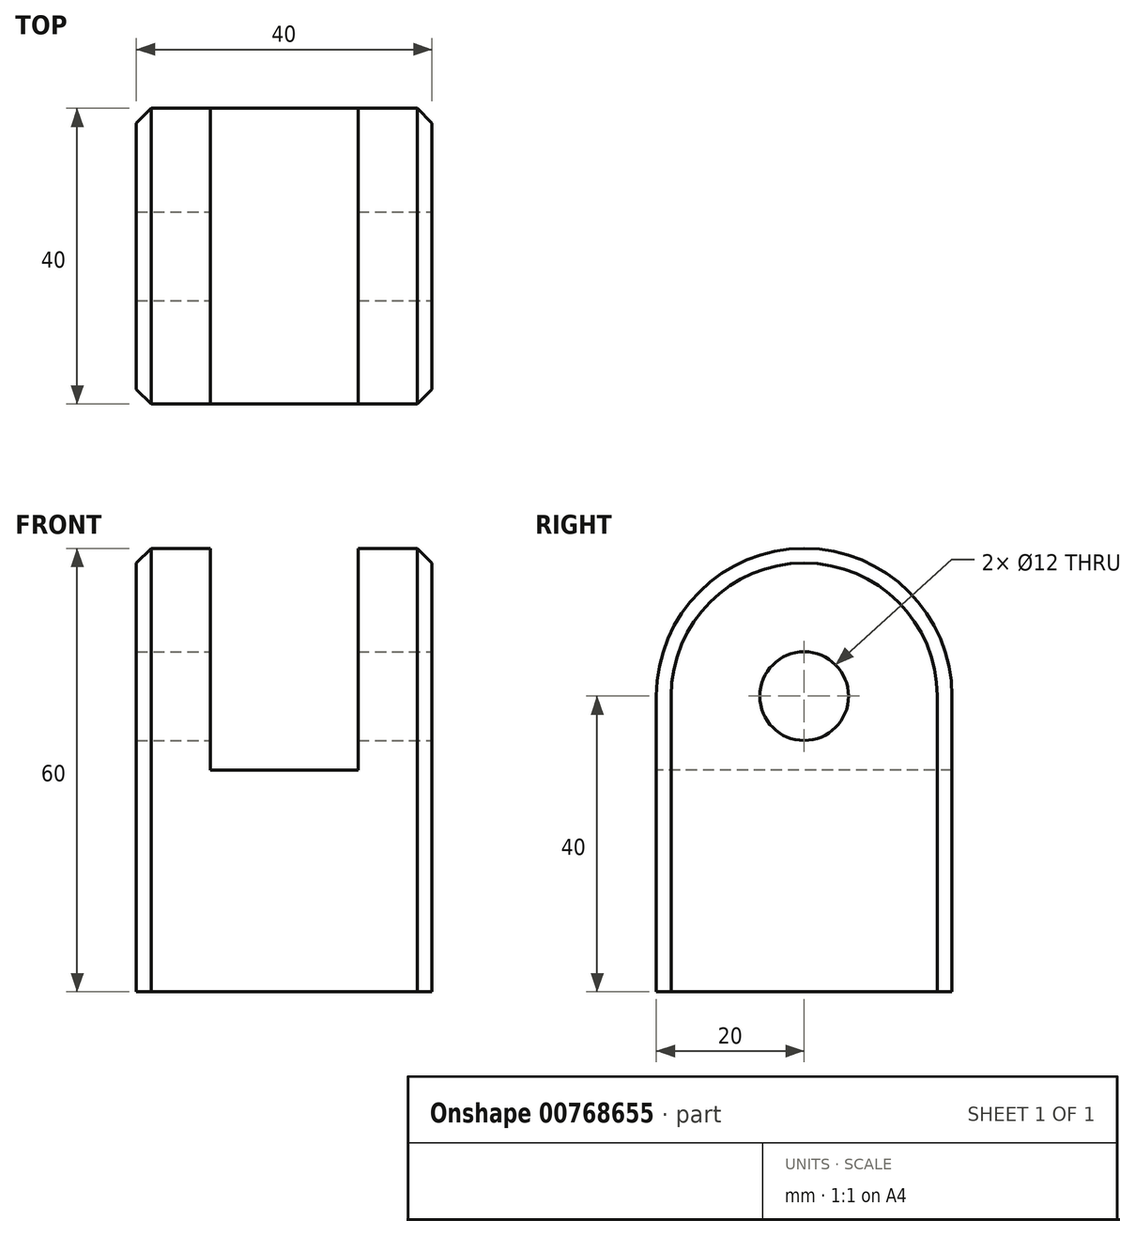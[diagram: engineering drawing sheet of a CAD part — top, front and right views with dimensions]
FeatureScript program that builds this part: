
annotation { "Feature Type Name" : "Feature", "Feature Type Description" : "" }
export const myFeature = defineFeature(function(context is Context, id is Id, definition is map)
    precondition{}
    {
        {
            var Q0;
            Q0=qCreatedBy(makeId("Top.planeOp"),FACE);
            var sketch = newSketch(context, id + "F0", { "sketchPlane" : qUnion([Q0])});
            skLineSegment(sketch, "E0.bottom", {"start": v(20, -20) * mm, "end": v(-20, -20) * mm});
            skLineSegment(sketch, "E0.top", {"start": v(20, 20) * mm, "end": v(-20, 20) * mm});
            skLineSegment(sketch, "E0.left", {"start": v(20, -20) * mm, "end": v(20, 20) * mm});
            skLineSegment(sketch, "E0.right", {"start": v(-20, -20) * mm, "end": v(-20, 20) * mm});
            skPoint(sketch, "E0.middle", {"position": v(0, 0) * mm});
            skSolve(sketch);
        }
        {
            var Q0;
            Q0 = qSketchRegion(id + "F0", true);
            extrude(context, id + "F1", {"entities" : qUnion([Q0]), "depth" : 60 * mm, "offsetDistance" : 25 * mm});
        }
        {
            var Q0;
            Q0=makeQuery(id+"F1.opExtrude","CAP_FACE",FACE,{"disambiguationData":[OSD([sQuery(id+"F0.wireOp",EDGE,"E0.bottom"),sQuery(id+"F0.wireOp",EDGE,"E0.top"),sQuery(id+"F0.wireOp",EDGE,"E0.left"),sQuery(id+"F0.wireOp",EDGE,"E0.right")])],"isStart":false});
            var sketch = newSketch(context, id + "F2", { "sketchPlane" : qUnion([Q0])});
            skLineSegment(sketch, "E1.bottom", {"start": v(-10, 20) * mm, "end": v(10, 20) * mm});
            skLineSegment(sketch, "E1.top", {"start": v(-10, -20) * mm, "end": v(10, -20) * mm});
            skLineSegment(sketch, "E1.left", {"start": v(-10, 20) * mm, "end": v(-10, -20) * mm});
            skLineSegment(sketch, "E1.right", {"start": v(10, 20) * mm, "end": v(10, -20) * mm});
            skLineSegment(sketch, "E2", {"start": v(-20, 0) * mm, "end": v(-10, 0) * mm, "construction": true});
            skLineSegment(sketch, "E3", {"start": v(-10, 0) * mm, "end": v(10, 0) * mm, "construction": true});
            skLineSegment(sketch, "E4", {"start": v(10, 0) * mm, "end": v(20, 0) * mm, "construction": true});
            skSolve(sketch);
        }
        {
            var Q0;
            Q0=makeQuery(id+"F2.imprint","IMPRINT",FACE,{"disambiguationData":[TD([[makeQuery(id+"F2.imprint","IMPRINT",EDGE,{"derivedFrom":sQuery(id+"F2.wireOp",EDGE,"E1.bottom")}),1.0]])]});
            extrude(context, id + "F3", {"entities" : qUnion([Q0]), "operationType" : NewBodyOperationType.REMOVE, "oppositeDirection" : true, "depth" : 30 * mm, "offsetDistance" : 25 * mm});
        }
        {
            var Q0;
            Q0=makeQuery(id+"F1.opExtrude","CAP_EDGE",EDGE,{"disambiguationData":[OSD([sQuery(id+"F0.wireOp",EDGE,"E0.bottom")])],"isStart":false});
            var Q1;
            Q1=makeQuery(id+"F1.opExtrude","CAP_EDGE",EDGE,{"disambiguationData":[OSD([sQuery(id+"F0.wireOp",EDGE,"E0.top")])],"isStart":false});
            fillet(context, id + "F4", {"entities" : qUnion([Q0, Q1]), "radius" : 20 * mm, "tangentPropagation" : true, "allowEdgeOverflow" : false});
        }
        {
            var Q0;
            Q0=makeQuery(id+"F1.opExtrude","SWEPT_EDGE",EDGE,{"disambiguationData":[OSD([sQuery(id+"F0.wireOp",EDGE,"E0.bottom"),sQuery(id+"F0.wireOp",EDGE,"E0.right")])]});
            var Q1;
            {var subQ0=sQuery(id+"F0.wireOp",EDGE,"E0.right");var subQ1=makeQuery(id+"F1.opExtrude","SWEPT_FACE",FACE,{"disambiguationData":[OSD([subQ0])]});var subQ2=sQuery(id+"F0.wireOp",EDGE,"E0.bottom");Q1=makeQuery(id+"F4.opFillet","BLEND_EDGE",EDGE,{"blendedFrom":[makeQuery(id+"F3.boolean.opBoolean","SPLIT",EDGE,{"disambiguationData":[TD([subQ1])],"derivedFrom":makeQuery(id+"F1.opExtrude","CAP_EDGE",EDGE,{"disambiguationData":[OSD([subQ2])],"isStart":false})}),subQ1],"blendedInto":[subQ1]});}
            var Q2;
            {var subQ0=sQuery(id+"F0.wireOp",EDGE,"E0.left");var subQ1=makeQuery(id+"F1.opExtrude","SWEPT_FACE",FACE,{"disambiguationData":[OSD([subQ0])]});var subQ2=sQuery(id+"F0.wireOp",EDGE,"E0.bottom");Q2=makeQuery(id+"F4.opFillet","BLEND_EDGE",EDGE,{"blendedFrom":[makeQuery(id+"F3.boolean.opBoolean","SPLIT",EDGE,{"disambiguationData":[TD([subQ1])],"derivedFrom":makeQuery(id+"F1.opExtrude","CAP_EDGE",EDGE,{"disambiguationData":[OSD([subQ2])],"isStart":false})}),subQ1],"blendedInto":[subQ1]});}
            chamfer(context, id + "F5", {"entities" : qUnion([Q0, Q1, Q2]), "width" : 2 * mm, "tangentPropagation" : true});
        }
        {
            var Q0;
            Q0=makeQuery(id+"F1.opExtrude","SWEPT_FACE",FACE,{"disambiguationData":[OSD([sQuery(id+"F0.wireOp",EDGE,"E0.left")])]});
            var sketch = newSketch(context, id + "F6", { "sketchPlane" : qUnion([Q0])});
            skCircle(sketch, "E5", {"center": v(0, 40) * mm, "radius": 6 * mm});
            skSolve(sketch);
        }
        {
            var Q0;
            Q0=makeQuery(id+"F6.imprint","IMPRINT",FACE,{"disambiguationData":[TD([[makeQuery(id+"F6.imprint","IMPRINT",EDGE,{"derivedFrom":sQuery(id+"F6.wireOp",EDGE,"E5")}),1.0]])]});
            extrude(context, id + "F7", {"entities" : qUnion([Q0]), "operationType" : NewBodyOperationType.REMOVE, "oppositeDirection" : true, "depth" : 56.6 * mm, "offsetDistance" : 25 * mm, "hasSecondDirection" : true, "secondDirectionOppositeDirection" : false, "secondDirectionDepth" : 25 * mm});
        }
    });
